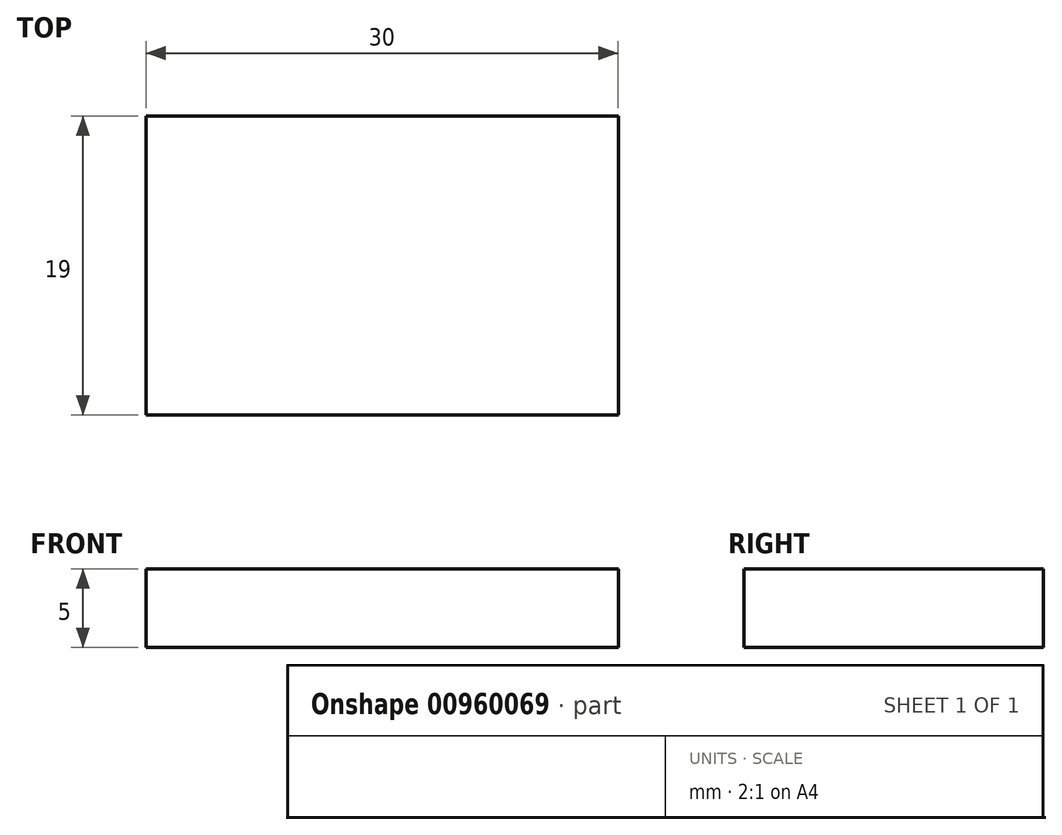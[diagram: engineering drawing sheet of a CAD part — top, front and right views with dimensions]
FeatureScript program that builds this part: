
annotation { "Feature Type Name" : "Feature", "Feature Type Description" : "" }
export const myFeature = defineFeature(function(context is Context, id is Id, definition is map)
    precondition{}
    {
        {
            var Q0;
            Q0=qCreatedBy(makeId("Front.planeOp"),FACE);
            var sketch = newSketch(context, id + "F0", { "sketchPlane" : qUnion([Q0])});
            skLineSegment(sketch, "E0.bottom", {"start": v(-6.9, -5.13) * mm, "end": v(23.1, -5.13) * mm});
            skLineSegment(sketch, "E0.top", {"start": v(-6.9, -10.13) * mm, "end": v(23.1, -10.13) * mm});
            skLineSegment(sketch, "E0.left", {"start": v(-6.9, -5.13) * mm, "end": v(-6.9, -10.13) * mm});
            skLineSegment(sketch, "E0.right", {"start": v(23.1, -5.13) * mm, "end": v(23.1, -10.13) * mm});
            skSolve(sketch);
        }
        {
            var Q0;
            Q0=makeQuery(id+"F0.imprint","IMPRINT",FACE,{"disambiguationData":[TD([[makeQuery(id+"F0.imprint","IMPRINT",EDGE,{"derivedFrom":sQuery(id+"F0.wireOp",EDGE,"E0.bottom")}),-1.0]])]});
            extrude(context, id + "F1", {"entities" : qUnion([Q0]), "depth" : 19 * mm, "offsetDistance" : 25 * mm});
        }
    });
